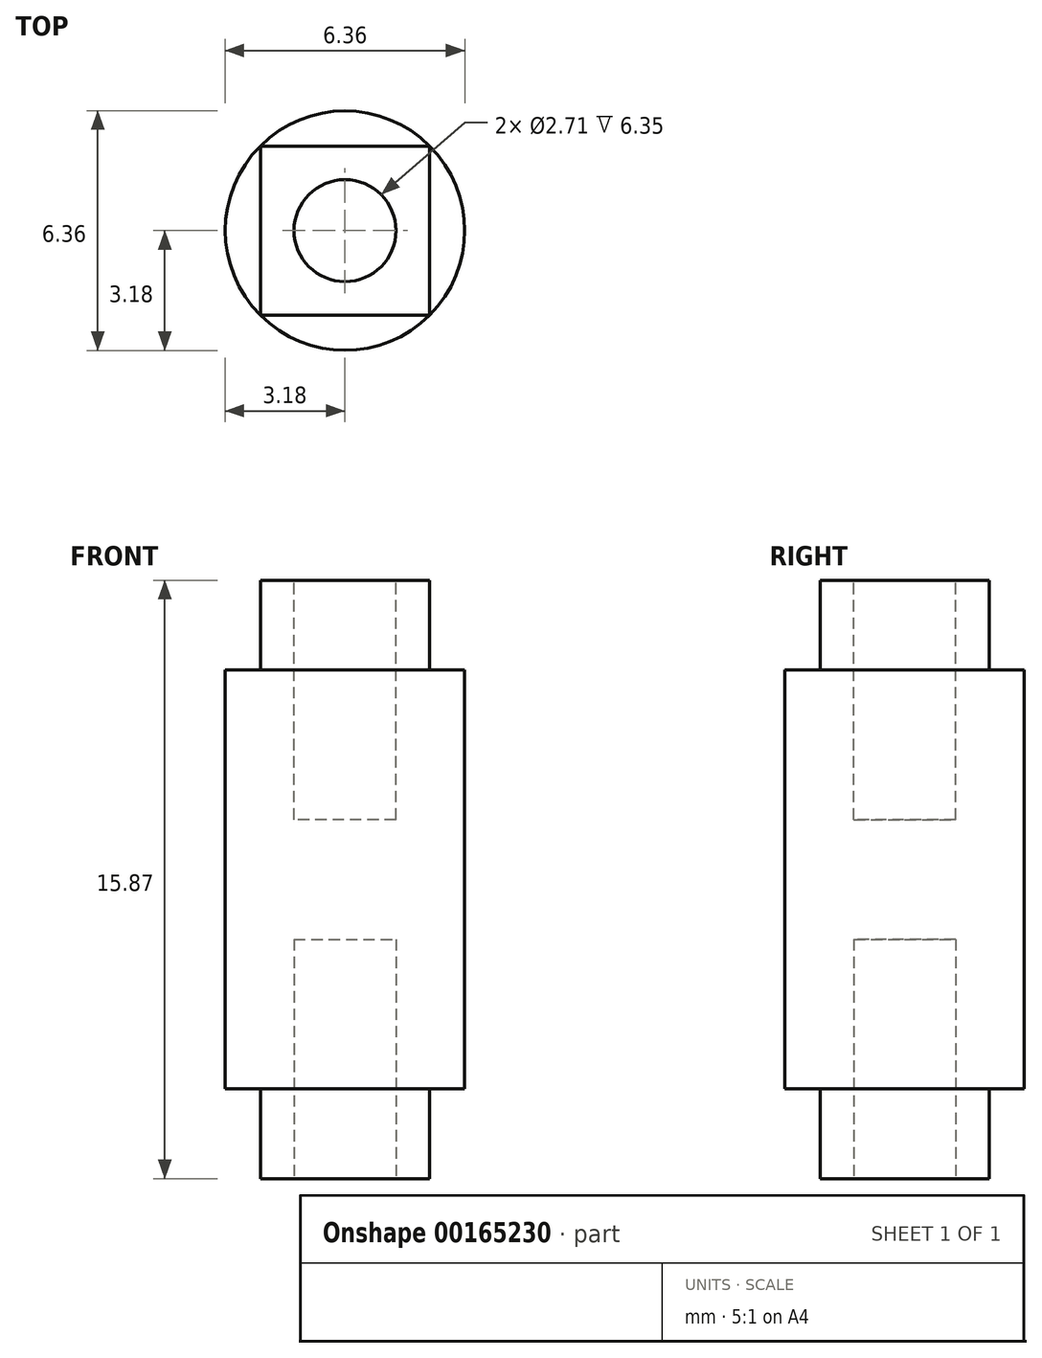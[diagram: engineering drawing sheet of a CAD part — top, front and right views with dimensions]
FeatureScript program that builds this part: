
annotation { "Feature Type Name" : "Feature", "Feature Type Description" : "" }
export const myFeature = defineFeature(function(context is Context, id is Id, definition is map)
    precondition{}
    {
        {
            var Q0;
            Q0=qCreatedBy(makeId("Top.planeOp"),FACE);
            var sketch = newSketch(context, id + "F0", { "sketchPlane" : qUnion([Q0])});
            skCircle(sketch, "E0", {"center": v(0, 0) * mm, "radius": 3.18 * mm});
            skSolve(sketch);
        }
        {
            var Q0;
            Q0 = qSketchRegion(id + "F0", true);
            extrude(context, id + "F1", {"entities" : qUnion([Q0]), "depth" : 11.1 * mm});
        }
        {
            var Q0;
            Q0=makeQuery(id+"F1.opExtrude","CAP_FACE",FACE,{"disambiguationData":[OSD([sQuery(id+"F0.wireOp",EDGE,"E0")])],"isStart":false});
            cPlane(context, id + "F2", {"entities" : qUnion([Q0]), "cplaneType" : CPlaneType.OFFSET, "offset" : 2.38 * mm, "width" : 152.4 * mm, "height" : 152.4 * mm});
        }
        {
            var Q0;
            Q0=makeQuery(id+"F1.opExtrude","CAP_FACE",FACE,{"disambiguationData":[OSD([sQuery(id+"F0.wireOp",EDGE,"E0")])],"isStart":true});
            var sketch = newSketch(context, id + "F3", { "sketchPlane" : qUnion([Q0])});
            skLineSegment(sketch, "E1.bottom", {"start": v(-2.25, 2.25) * mm, "end": v(2.25, 2.25) * mm});
            skLineSegment(sketch, "E1.top", {"start": v(-2.25, -2.25) * mm, "end": v(2.25, -2.25) * mm});
            skLineSegment(sketch, "E1.left", {"start": v(-2.25, 2.25) * mm, "end": v(-2.25, -2.25) * mm});
            skLineSegment(sketch, "E1.right", {"start": v(2.25, 2.25) * mm, "end": v(2.25, -2.25) * mm});
            skPoint(sketch, "E1.middle", {"position": v(0, 0) * mm});
            skSolve(sketch);
        }
        {
            var Q0;
            Q0 = qSketchRegion(id + "F3", true);
            var Q1;
            Q1=qCreatedBy(id+"F2.planeOp",FACE);
            extrude(context, id + "F4", {"entities" : qUnion([Q0]), "operationType" : NewBodyOperationType.ADD, "depth" : 2.38 * mm, "hasSecondDirection" : true, "secondDirectionBound" : SecondDirectionBoundingType.UP_TO_SURFACE, "secondDirectionOppositeDirection" : true, "secondDirectionBoundEntityFace" : qUnion([Q1]), "secondDirectionDepth" : 25.4 * mm});
        }
        {
            var Q0;
            Q0=makeQuery(id+"F4.opExtrude","CAP_FACE",FACE,{"disambiguationData":[OSD([sQuery(id+"F3.wireOp",EDGE,"E1.bottom"),sQuery(id+"F3.wireOp",EDGE,"E1.top"),sQuery(id+"F3.wireOp",EDGE,"E1.left"),sQuery(id+"F3.wireOp",EDGE,"E1.right")])],"isStart":true});
            var sketch = newSketch(context, id + "F5", { "sketchPlane" : qUnion([Q0])});
            skCircle(sketch, "E2", {"center": v(0, 0) * mm, "radius": 1.35 * mm});
            skSolve(sketch);
        }
        {
            var Q0;
            Q0 = qSketchRegion(id + "F5", true);
            extrude(context, id + "F6", {"entities" : qUnion([Q0]), "operationType" : NewBodyOperationType.REMOVE, "oppositeDirection" : true, "depth" : 6.35 * mm});
        }
        {
            var Q0;
            Q0=makeQuery(id+"F4.opExtrude","CAP_FACE",FACE,{"disambiguationData":[OSD([sQuery(id+"F3.wireOp",EDGE,"E1.bottom"),sQuery(id+"F3.wireOp",EDGE,"E1.top"),sQuery(id+"F3.wireOp",EDGE,"E1.left"),sQuery(id+"F3.wireOp",EDGE,"E1.right")])],"isStart":false});
            var sketch = newSketch(context, id + "F7", { "sketchPlane" : qUnion([Q0])});
            skCircle(sketch, "E3", {"center": v(0, 0) * mm, "radius": 1.35 * mm});
            skSolve(sketch);
        }
        {
            var Q0;
            Q0 = qSketchRegion(id + "F7", true);
            extrude(context, id + "F8", {"entities" : qUnion([Q0]), "operationType" : NewBodyOperationType.REMOVE, "oppositeDirection" : true, "depth" : 6.35 * mm});
        }
    });
